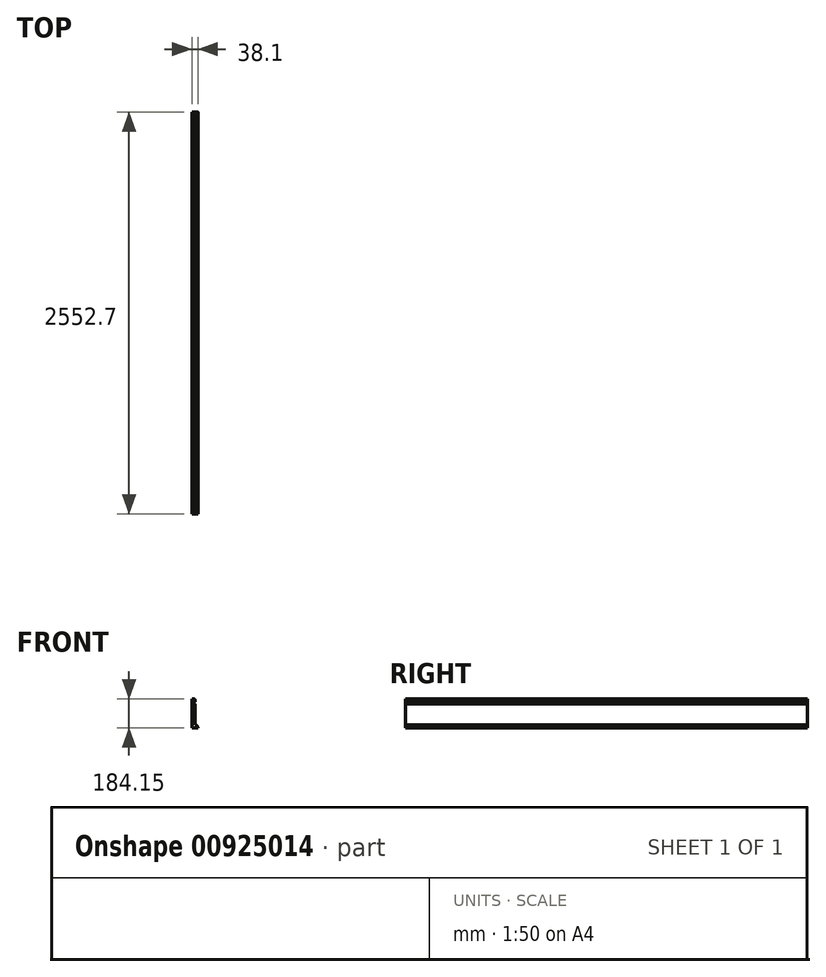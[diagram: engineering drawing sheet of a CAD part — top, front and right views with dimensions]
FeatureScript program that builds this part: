
annotation { "Feature Type Name" : "Feature", "Feature Type Description" : "" }
export const myFeature = defineFeature(function(context is Context, id is Id, definition is map)
    precondition{}
    {
        {
            var Q0;
            Q0=qCreatedBy(makeId("Front.planeOp"),FACE);
            var sketch = newSketch(context, id + "F0", { "sketchPlane" : qUnion([Q0])});
            skLineSegment(sketch, "E0.bottom", {"start": v(0, 0) * mm, "end": v(19.05, 0) * mm});
            skLineSegment(sketch, "E0.top", {"start": v(0, 184.15) * mm, "end": v(12.7, 184.15) * mm});
            skLineSegment(sketch, "E0.left", {"start": v(0, 0) * mm, "end": v(0, 184.15) * mm});
            skLineSegment(sketch, "E0.right", {"start": v(19.05, 0) * mm, "end": v(19.05, 152.4) * mm});
            skArc(sketch, "E1", {"start": v(19.05, 165.1) * mm, "mid": v(12.7, 158.75) * mm, "end": v(19.05, 152.4) * mm});
            skPoint(sketch, "E2.visualSharp", {"position": v(19.05, 184.15) * mm});
            skArc(sketch, "E2.filletArc", {"start": v(19.05, 177.8) * mm, "mid": v(17.2, 182.3) * mm, "end": v(12.7, 184.15) * mm});
            skArc(sketch, "E3", {"start": v(38.1, 0) * mm, "mid": v(32.52, 13.47) * mm, "end": v(19.05, 19.05) * mm});
            skLineSegment(sketch, "E4", {"start": v(19.05, 0) * mm, "end": v(38.1, 0) * mm});
            skLineSegment(sketch, "E5.trimOffspring", {"start": v(19.05, 165.1) * mm, "end": v(19.05, 177.8) * mm});
            skSolve(sketch);
        }
        {
            var Q0;
            {var subQ1=sQuery(id+"F0.wireOp",EDGE,"E0.bottom");Q0=makeQuery(id+"F0.imprint","IMPRINT",FACE,{"disambiguationData":[TD([[makeQuery(id+"F0.imprint","IMPRINT",EDGE,{"derivedFrom":subQ1}),1.0]])]});}
            var Q1;
            {var subQ2=sQuery(id+"F0.wireOp",EDGE,"E3");Q1=makeQuery(id+"F0.imprint","IMPRINT",FACE,{"disambiguationData":[TD([[makeQuery(id+"F0.imprint","IMPRINT",EDGE,{"derivedFrom":subQ2}),1.0]])]});}
            extrude(context, id + "F1", {"entities" : qUnion([Q0, Q1]), "oppositeDirection" : true, "depth" : 2552.7 * mm, "offsetDistance" : 25.4 * mm});
        }
    });
